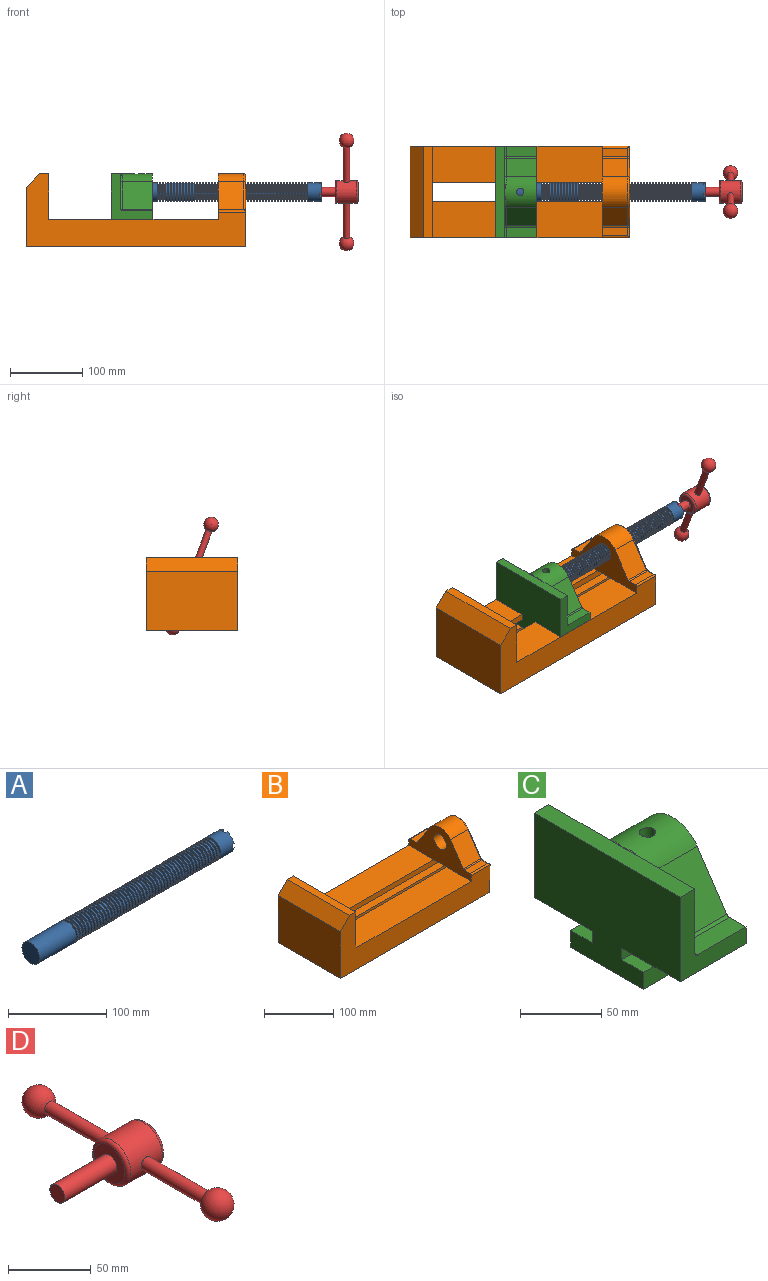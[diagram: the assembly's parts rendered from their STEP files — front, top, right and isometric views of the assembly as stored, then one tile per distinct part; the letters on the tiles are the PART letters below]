
ASSEMBLY  parts=4 mates=3
PART A: 220 faces, bbox 279.4x25.4x25.4 mm
  f0: cylinder r=12.7mm len=25.4mm, axis (-1,0,0), area 1468.2mm2, adj f1,f2,f3,f5,f7,f208,f209,f210
  f1: plane 9.9x9.9mm, normal (1,0,0), area 62.3mm2, adj f0,f4,f213,f216
  f2: plane 9.9x9.9mm, normal (1,0,0), area 62.3mm2, adj f0,f4,f210,f218
  f3: plane 9.9x9.9mm, normal (1,0,0), area 62.3mm2, adj f0,f4,f209,f212
  f4: cylinder r=6.35mm len=25.4mm, axis (1,0,0), area 960.3mm2, adj f1,f2,f3,f5,f6,f208,f209,f210
  f5: plane 9.9x9.9mm, normal (1,0,0), area 62.3mm2, adj f0,f4,f215,f217
  f6: plane 12.7x12.7mm, normal (1,0,0), area 126.7mm2, adj f4
  f7: cone r=12.7mm half-angle=76deg, axis (1,0,0), area 188mm2, adj f0,f9
  f8: cone r=10.16mm half-angle=76deg, axis (-1,0,0), area 188mm2, adj f9,f10
  f9: cylinder r=10.16mm len=20.32mm, axis (1,0,0), area 81.1mm2, adj f7,f8
  f10: cylinder r=12.7mm len=25.4mm, axis (-1,0,0), area 131.7mm2, adj f8,f11
  f11: cone r=12.7mm half-angle=76deg, axis (1,0,0), area 188mm2, adj f10,f13
  f12: cone r=10.16mm half-angle=76deg, axis (-1,0,0), area 188mm2, adj f13,f14
  f13: cylinder r=10.16mm len=20.32mm, axis (1,0,0), area 81.1mm2, adj f11,f12
  f14: cylinder r=12.7mm len=25.4mm, axis (-1,0,0), area 131.7mm2, adj f12,f15
  f15: cone r=12.7mm half-angle=76deg, axis (1,0,0), area 188mm2, adj f14,f17
  f16: cone r=10.16mm half-angle=76deg, axis (-1,0,0), area 188mm2, adj f17,f18
  f17: cylinder r=10.16mm len=20.32mm, axis (1,0,0), area 81.1mm2, adj f15,f16
  f18: cylinder r=12.7mm len=25.4mm, axis (-1,0,0), area 131.7mm2, adj f16,f19
  f19: cone r=12.7mm half-angle=76deg, axis (1,0,0), area 188mm2, adj f18,f21
  f20: cone r=10.16mm half-angle=76deg, axis (-1,0,0), area 188mm2, adj f21,f22
  f21: cylinder r=10.16mm len=20.32mm, axis (1,0,0), area 81.1mm2, adj f19,f20
  f22: cylinder r=12.7mm len=25.4mm, axis (-1,0,0), area 131.7mm2, adj f20,f23
  f23: cone r=12.7mm half-angle=76deg, axis (1,0,0), area 188mm2, adj f22,f25
  f24: cone r=10.16mm half-angle=76deg, axis (-1,0,0), area 188mm2, adj f25,f26
  f25: cylinder r=10.16mm len=20.32mm, axis (1,0,0), area 81.1mm2, adj f23,f24
  f26: cylinder r=12.7mm len=25.4mm, axis (-1,0,0), area 131.7mm2, adj f24,f27
  f27: cone r=12.7mm half-angle=76deg, axis (1,0,0), area 188mm2, adj f26,f29
  f28: cone r=10.16mm half-angle=76deg, axis (-1,0,0), area 188mm2, adj f29,f30
  f29: cylinder r=10.16mm len=20.32mm, axis (1,0,0), area 81.1mm2, adj f27,f28
  f30: cylinder r=12.7mm len=25.4mm, axis (-1,0,0), area 131.7mm2, adj f28,f31
  f31: cone r=12.7mm half-angle=76deg, axis (1,0,0), area 188mm2, adj f30,f33
  f32: cone r=10.16mm half-angle=76deg, axis (-1,0,0), area 188mm2, adj f33,f34
  f33: cylinder r=10.16mm len=20.32mm, axis (1,0,0), area 81.1mm2, adj f31,f32
  f34: cylinder r=12.7mm len=25.4mm, axis (-1,0,0), area 131.7mm2, adj f32,f35
  f35: cone r=12.7mm half-angle=76deg, axis (1,0,0), area 188mm2, adj f34,f37
  f36: cone r=10.16mm half-angle=76deg, axis (-1,0,0), area 188mm2, adj f37,f38
  f37: cylinder r=10.16mm len=20.32mm, axis (1,0,0), area 81.1mm2, adj f35,f36
  f38: cylinder r=12.7mm len=25.4mm, axis (-1,0,0), area 131.7mm2, adj f36,f39
  f39: cone r=12.7mm half-angle=76deg, axis (1,0,0), area 188mm2, adj f38,f41
  f40: cone r=10.16mm half-angle=76deg, axis (-1,0,0), area 188mm2, adj f41,f42
  f41: cylinder r=10.16mm len=20.32mm, axis (1,0,0), area 81.1mm2, adj f39,f40
  f42: cylinder r=12.7mm len=25.4mm, axis (-1,0,0), area 131.7mm2, adj f40,f43
  f43: cone r=12.7mm half-angle=76deg, axis (1,0,0), area 188mm2, adj f42,f45
  f44: cone r=10.16mm half-angle=76deg, axis (-1,0,0), area 188mm2, adj f45,f46
  f45: cylinder r=10.16mm len=20.32mm, axis (1,0,0), area 81.1mm2, adj f43,f44
  f46: cylinder r=12.7mm len=25.4mm, axis (-1,0,0), area 131.7mm2, adj f44,f47
  f47: cone r=12.7mm half-angle=76deg, axis (1,0,0), area 188mm2, adj f46,f49
  f48: cone r=10.16mm half-angle=76deg, axis (-1,0,0), area 188mm2, adj f49,f50
  f49: cylinder r=10.16mm len=20.32mm, axis (1,0,0), area 81.1mm2, adj f47,f48
  f50: cylinder r=12.7mm len=25.4mm, axis (-1,0,0), area 131.7mm2, adj f48,f51
  f51: cone r=12.7mm half-angle=76deg, axis (1,0,0), area 188mm2, adj f50,f53
  f52: cone r=10.16mm half-angle=76deg, axis (-1,0,0), area 188mm2, adj f53,f54
  f53: cylinder r=10.16mm len=20.32mm, axis (1,0,0), area 81.1mm2, adj f51,f52
  f54: cylinder r=12.7mm len=25.4mm, axis (-1,0,0), area 131.7mm2, adj f52,f55
  f55: cone r=12.7mm half-angle=76deg, axis (1,0,0), area 188mm2, adj f54,f57
  f56: cone r=10.16mm half-angle=76deg, axis (-1,0,0), area 188mm2, adj f57,f58
  f57: cylinder r=10.16mm len=20.32mm, axis (1,0,0), area 81.1mm2, adj f55,f56
  f58: cylinder r=12.7mm len=25.4mm, axis (-1,0,0), area 131.7mm2, adj f56,f59
  f59: cone r=12.7mm half-angle=76deg, axis (1,0,0), area 188mm2, adj f58,f61
  f60: cone r=10.16mm half-angle=76deg, axis (-1,0,0), area 188mm2, adj f61,f62
  f61: cylinder r=10.16mm len=20.32mm, axis (1,0,0), area 81.1mm2, adj f59,f60
  f62: cylinder r=12.7mm len=25.4mm, axis (-1,0,0), area 131.7mm2, adj f60,f63
  f63: cone r=12.7mm half-angle=76deg, axis (1,0,0), area 188mm2, adj f62,f65
  f64: cone r=10.16mm half-angle=76deg, axis (-1,0,0), area 188mm2, adj f65,f66
  f65: cylinder r=10.16mm len=20.32mm, axis (1,0,0), area 81.1mm2, adj f63,f64
  f66: cylinder r=12.7mm len=25.4mm, axis (-1,0,0), area 131.7mm2, adj f64,f67
  f67: cone r=12.7mm half-angle=76deg, axis (1,0,0), area 188mm2, adj f66,f69
  f68: cone r=10.16mm half-angle=76deg, axis (-1,0,0), area 188mm2, adj f69,f70
  f69: cylinder r=10.16mm len=20.32mm, axis (1,0,0), area 81.1mm2, adj f67,f68
  f70: cylinder r=12.7mm len=25.4mm, axis (-1,0,0), area 131.7mm2, adj f68,f71
  f71: cone r=12.7mm half-angle=76deg, axis (1,0,0), area 188mm2, adj f70,f73
  f72: cone r=10.16mm half-angle=76deg, axis (-1,0,0), area 188mm2, adj f73,f74
  f73: cylinder r=10.16mm len=20.32mm, axis (1,0,0), area 81.1mm2, adj f71,f72
  f74: cylinder r=12.7mm len=25.4mm, axis (-1,0,0), area 131.7mm2, adj f72,f75
  f75: cone r=12.7mm half-angle=76deg, axis (1,0,0), area 188mm2, adj f74,f77
  f76: cone r=10.16mm half-angle=76deg, axis (-1,0,0), area 188mm2, adj f77,f78
  f77: cylinder r=10.16mm len=20.32mm, axis (1,0,0), area 81.1mm2, adj f75,f76
  f78: cylinder r=12.7mm len=25.4mm, axis (-1,0,0), area 131.7mm2, adj f76,f79
  f79: cone r=12.7mm half-angle=76deg, axis (1,0,0), area 188mm2, adj f78,f81
  f80: cone r=10.16mm half-angle=76deg, axis (-1,0,0), area 188mm2, adj f81,f82
  f81: cylinder r=10.16mm len=20.32mm, axis (1,0,0), area 81.1mm2, adj f79,f80
  f82: cylinder r=12.7mm len=25.4mm, axis (-1,0,0), area 131.7mm2, adj f80,f83
  f83: cone r=12.7mm half-angle=76deg, axis (1,0,0), area 188mm2, adj f82,f85
  f84: cone r=10.16mm half-angle=76deg, axis (-1,0,0), area 188mm2, adj f85,f86
  f85: cylinder r=10.16mm len=20.32mm, axis (1,0,0), area 81.1mm2, adj f83,f84
  f86: cylinder r=12.7mm len=25.4mm, axis (-1,0,0), area 131.7mm2, adj f84,f87
  f87: cone r=12.7mm half-angle=76deg, axis (1,0,0), area 188mm2, adj f86,f89
  f88: cone r=10.16mm half-angle=76deg, axis (-1,0,0), area 188mm2, adj f89,f90
  f89: cylinder r=10.16mm len=20.32mm, axis (1,0,0), area 81.1mm2, adj f87,f88
  f90: cylinder r=12.7mm len=25.4mm, axis (-1,0,0), area 131.7mm2, adj f88,f91
  f91: cone r=12.7mm half-angle=76deg, axis (1,0,0), area 188mm2, adj f90,f93
  f92: cone r=10.16mm half-angle=76deg, axis (-1,0,0), area 188mm2, adj f93,f94
  f93: cylinder r=10.16mm len=20.32mm, axis (1,0,0), area 81.1mm2, adj f91,f92
  f94: cylinder r=12.7mm len=25.4mm, axis (-1,0,0), area 131.7mm2, adj f92,f95
  f95: cone r=12.7mm half-angle=76deg, axis (1,0,0), area 188mm2, adj f94,f97
  f96: cone r=10.16mm half-angle=76deg, axis (-1,0,0), area 188mm2, adj f97,f98
  f97: cylinder r=10.16mm len=20.32mm, axis (1,0,0), area 81.1mm2, adj f95,f96
  f98: cylinder r=12.7mm len=25.4mm, axis (-1,0,0), area 131.7mm2, adj f96,f99
  f99: cone r=12.7mm half-angle=76deg, axis (1,0,0), area 188mm2, adj f98,f101
  f100: cone r=10.16mm half-angle=76deg, axis (-1,0,0), area 188mm2, adj f101,f102
  f101: cylinder r=10.16mm len=20.32mm, axis (1,0,0), area 81.1mm2, adj f99,f100
  f102: cylinder r=12.7mm len=25.4mm, axis (-1,0,0), area 131.7mm2, adj f100,f103
  f103: cone r=12.7mm half-angle=76deg, axis (1,0,0), area 188mm2, adj f102,f105
  f104: cone r=10.16mm half-angle=76deg, axis (-1,0,0), area 188mm2, adj f105,f106
  f105: cylinder r=10.16mm len=20.32mm, axis (1,0,0), area 81.1mm2, adj f103,f104
  f106: cylinder r=12.7mm len=25.4mm, axis (-1,0,0), area 131.7mm2, adj f104,f107
  f107: cone r=12.7mm half-angle=76deg, axis (1,0,0), area 188mm2, adj f106,f109
  f108: cone r=10.16mm half-angle=76deg, axis (-1,0,0), area 188mm2, adj f109,f110
  f109: cylinder r=10.16mm len=20.32mm, axis (1,0,0), area 81.1mm2, adj f107,f108
  f110: cylinder r=12.7mm len=25.4mm, axis (-1,0,0), area 131.7mm2, adj f108,f111
  f111: cone r=12.7mm half-angle=76deg, axis (1,0,0), area 188mm2, adj f110,f113
  f112: cone r=10.16mm half-angle=76deg, axis (-1,0,0), area 188mm2, adj f113,f114
  f113: cylinder r=10.16mm len=20.32mm, axis (1,0,0), area 81.1mm2, adj f111,f112
  f114: cylinder r=12.7mm len=25.4mm, axis (-1,0,0), area 131.7mm2, adj f112,f115
  f115: cone r=12.7mm half-angle=76deg, axis (1,0,0), area 188mm2, adj f114,f117
  f116: cone r=10.16mm half-angle=76deg, axis (-1,0,0), area 188mm2, adj f117,f118
  f117: cylinder r=10.16mm len=20.32mm, axis (1,0,0), area 81.1mm2, adj f115,f116
  f118: cylinder r=12.7mm len=25.4mm, axis (-1,0,0), area 131.7mm2, adj f116,f119
  f119: cone r=12.7mm half-angle=76deg, axis (1,0,0), area 188mm2, adj f118,f121
  f120: cone r=10.16mm half-angle=76deg, axis (-1,0,0), area 188mm2, adj f121,f122
  f121: cylinder r=10.16mm len=20.32mm, axis (1,0,0), area 81.1mm2, adj f119,f120
  f122: cylinder r=12.7mm len=25.4mm, axis (-1,0,0), area 131.7mm2, adj f120,f123
  f123: cone r=12.7mm half-angle=76deg, axis (1,0,0), area 188mm2, adj f122,f125
  f124: cone r=10.16mm half-angle=76deg, axis (-1,0,0), area 188mm2, adj f125,f126
  f125: cylinder r=10.16mm len=20.32mm, axis (1,0,0), area 81.1mm2, adj f123,f124
  f126: cylinder r=12.7mm len=25.4mm, axis (-1,0,0), area 131.7mm2, adj f124,f127
  f127: cone r=12.7mm half-angle=76deg, axis (1,0,0), area 188mm2, adj f126,f129
  f128: cone r=10.16mm half-angle=76deg, axis (-1,0,0), area 188mm2, adj f129,f130
  f129: cylinder r=10.16mm len=20.32mm, axis (1,0,0), area 81.1mm2, adj f127,f128
  f130: cylinder r=12.7mm len=25.4mm, axis (-1,0,0), area 131.7mm2, adj f128,f131
  f131: cone r=12.7mm half-angle=76deg, axis (1,0,0), area 188mm2, adj f130,f133
  f132: cone r=10.16mm half-angle=76deg, axis (-1,0,0), area 188mm2, adj f133,f134
  f133: cylinder r=10.16mm len=20.32mm, axis (1,0,0), area 81.1mm2, adj f131,f132
  f134: cylinder r=12.7mm len=25.4mm, axis (-1,0,0), area 131.7mm2, adj f132,f135
  f135: cone r=12.7mm half-angle=76deg, axis (1,0,0), area 188mm2, adj f134,f137
  f136: cone r=10.16mm half-angle=76deg, axis (-1,0,0), area 188mm2, adj f137,f138
  f137: cylinder r=10.16mm len=20.32mm, axis (1,0,0), area 81.1mm2, adj f135,f136
  f138: cylinder r=12.7mm len=25.4mm, axis (-1,0,0), area 131.7mm2, adj f136,f139
  f139: cone r=12.7mm half-angle=76deg, axis (1,0,0), area 188mm2, adj f138,f141
  f140: cone r=10.16mm half-angle=76deg, axis (-1,0,0), area 188mm2, adj f141,f142
  f141: cylinder r=10.16mm len=20.32mm, axis (1,0,0), area 81.1mm2, adj f139,f140
  f142: cylinder r=12.7mm len=25.4mm, axis (-1,0,0), area 131.7mm2, adj f140,f143
  f143: cone r=12.7mm half-angle=76deg, axis (1,0,0), area 188mm2, adj f142,f145
  f144: cone r=10.16mm half-angle=76deg, axis (-1,0,0), area 188mm2, adj f145,f146
  f145: cylinder r=10.16mm len=20.32mm, axis (1,0,0), area 81.1mm2, adj f143,f144
  f146: cylinder r=12.7mm len=25.4mm, axis (-1,0,0), area 131.7mm2, adj f144,f147
  f147: cone r=12.7mm half-angle=76deg, axis (1,0,0), area 188mm2, adj f146,f149
  f148: cone r=10.16mm half-angle=76deg, axis (-1,0,0), area 188mm2, adj f149,f150
  f149: cylinder r=10.16mm len=20.32mm, axis (1,0,0), area 81.1mm2, adj f147,f148
  f150: cylinder r=12.7mm len=25.4mm, axis (-1,0,0), area 131.7mm2, adj f148,f151
  f151: cone r=12.7mm half-angle=76deg, axis (1,0,0), area 188mm2, adj f150,f153
  f152: cone r=10.16mm half-angle=76deg, axis (-1,0,0), area 188mm2, adj f153,f154
  f153: cylinder r=10.16mm len=20.32mm, axis (1,0,0), area 81.1mm2, adj f151,f152
  f154: cylinder r=12.7mm len=25.4mm, axis (-1,0,0), area 131.7mm2, adj f152,f155
  f155: cone r=12.7mm half-angle=76deg, axis (1,0,0), area 188mm2, adj f154,f157
  f156: cone r=10.16mm half-angle=76deg, axis (-1,0,0), area 188mm2, adj f157,f158
  f157: cylinder r=10.16mm len=20.32mm, axis (1,0,0), area 81.1mm2, adj f155,f156
  f158: cylinder r=12.7mm len=25.4mm, axis (-1,0,0), area 131.7mm2, adj f156,f159
  f159: cone r=12.7mm half-angle=76deg, axis (1,0,0), area 188mm2, adj f158,f161
  f160: cone r=10.16mm half-angle=76deg, axis (-1,0,0), area 188mm2, adj f161,f162
  f161: cylinder r=10.16mm len=20.32mm, axis (1,0,0), area 81.1mm2, adj f159,f160
  f162: cylinder r=12.7mm len=25.4mm, axis (-1,0,0), area 131.7mm2, adj f160,f163
  f163: cone r=12.7mm half-angle=76deg, axis (1,0,0), area 188mm2, adj f162,f165
  f164: cone r=10.16mm half-angle=76deg, axis (-1,0,0), area 188mm2, adj f165,f166
  f165: cylinder r=10.16mm len=20.32mm, axis (1,0,0), area 81.1mm2, adj f163,f164
  f166: cylinder r=12.7mm len=25.4mm, axis (-1,0,0), area 131.7mm2, adj f164,f167
  f167: cone r=12.7mm half-angle=76deg, axis (1,0,0), area 188mm2, adj f166,f169
  f168: cone r=10.16mm half-angle=76deg, axis (-1,0,0), area 188mm2, adj f169,f170
  f169: cylinder r=10.16mm len=20.32mm, axis (1,0,0), area 81.1mm2, adj f167,f168
  f170: cylinder r=12.7mm len=25.4mm, axis (-1,0,0), area 131.7mm2, adj f168,f171
  f171: cone r=12.7mm half-angle=76deg, axis (1,0,0), area 188mm2, adj f170,f173
  f172: cone r=10.16mm half-angle=76deg, axis (-1,0,0), area 188mm2, adj f173,f174
  f173: cylinder r=10.16mm len=20.32mm, axis (1,0,0), area 81.1mm2, adj f171,f172
  f174: cylinder r=12.7mm len=25.4mm, axis (-1,0,0), area 131.7mm2, adj f172,f175
  f175: cone r=12.7mm half-angle=76deg, axis (1,0,0), area 188mm2, adj f174,f177
  f176: cone r=10.16mm half-angle=76deg, axis (-1,0,0), area 188mm2, adj f177,f178
  f177: cylinder r=10.16mm len=20.32mm, axis (1,0,0), area 81.1mm2, adj f175,f176
  f178: cylinder r=12.7mm len=25.4mm, axis (-1,0,0), area 131.7mm2, adj f176,f179
  f179: cone r=12.7mm half-angle=76deg, axis (1,0,0), area 188mm2, adj f178,f181
  f180: cone r=10.16mm half-angle=76deg, axis (-1,0,0), area 188mm2, adj f181,f182
  f181: cylinder r=10.16mm len=20.32mm, axis (1,0,0), area 81.1mm2, adj f179,f180
  f182: cylinder r=12.7mm len=25.4mm, axis (-1,0,0), area 131.7mm2, adj f180,f183
  f183: cone r=12.7mm half-angle=76deg, axis (1,0,0), area 188mm2, adj f182,f185
  f184: cone r=10.16mm half-angle=76deg, axis (-1,0,0), area 188mm2, adj f185,f186
  f185: cylinder r=10.16mm len=20.32mm, axis (1,0,0), area 81.1mm2, adj f183,f184
  f186: cylinder r=12.7mm len=25.4mm, axis (-1,0,0), area 131.7mm2, adj f184,f187
  f187: cone r=12.7mm half-angle=76deg, axis (1,0,0), area 188mm2, adj f186,f189
  f188: cone r=10.16mm half-angle=76deg, axis (-1,0,0), area 188mm2, adj f189,f190
  f189: cylinder r=10.16mm len=20.32mm, axis (1,0,0), area 81.1mm2, adj f187,f188
  f190: cylinder r=12.7mm len=25.4mm, axis (-1,0,0), area 131.7mm2, adj f188,f191
  f191: cone r=12.7mm half-angle=76deg, axis (1,0,0), area 188mm2, adj f190,f193
  f192: cone r=10.16mm half-angle=76deg, axis (-1,0,0), area 188mm2, adj f193,f194
  f193: cylinder r=10.16mm len=20.32mm, axis (1,0,0), area 81.1mm2, adj f191,f192
  f194: cylinder r=12.7mm len=25.4mm, axis (-1,0,0), area 131.7mm2, adj f192,f195
  f195: cone r=12.7mm half-angle=76deg, axis (1,0,0), area 188mm2, adj f194,f197
  f196: cone r=10.16mm half-angle=76deg, axis (-1,0,0), area 188mm2, adj f197,f198
  f197: cylinder r=10.16mm len=20.32mm, axis (1,0,0), area 81.1mm2, adj f195,f196
  f198: cylinder r=12.7mm len=25.4mm, axis (-1,0,0), area 131.7mm2, adj f196,f199
  f199: cone r=12.7mm half-angle=76deg, axis (1,0,0), area 188mm2, adj f198,f201
  f200: cone r=10.16mm half-angle=76deg, axis (-1,0,0), area 188mm2, adj f201,f202
  f201: cylinder r=10.16mm len=20.32mm, axis (1,0,0), area 81.1mm2, adj f199,f200
  f202: cylinder r=12.7mm len=25.4mm, axis (-1,0,0), area 131.7mm2, adj f200,f203
  f203: cone r=12.7mm half-angle=76deg, axis (1,0,0), area 188mm2, adj f202,f205
  f204: cone r=10.16mm half-angle=76deg, axis (-1,0,0), area 188mm2, adj f205,f207
  f205: cylinder r=10.16mm len=20.32mm, axis (1,0,0), area 81.1mm2, adj f203,f204
  f206: plane 25.4x25.4mm, normal (-1,0,0), area 506.7mm2, adj f207
  f207: cylinder r=12.7mm len=52.45mm, axis (-1,0,0), area 4185.4mm2, adj f204,f206
  f208: plane 6.88x5.08mm, normal (1,0,0), area 32.7mm2, adj f0,f4,f209,f210
  f209: plane 6.62x2.54mm, normal (0,-1,0), area 16.8mm2, adj f0,f3,f4,f208
  f210: plane 6.62x2.54mm, normal (0,1,0), area 16.8mm2, adj f0,f2,f4,f208
  f211: plane 6.88x5.08mm, normal (1,0,0), area 32.7mm2, adj f0,f4,f212,f213
  f212: plane 6.62x2.54mm, normal (0,0,1), area 16.8mm2, adj f0,f3,f4,f211
  f213: plane 6.62x2.54mm, normal (0,0,-1), area 16.8mm2, adj f0,f1,f4,f211
  f214: plane 6.88x5.08mm, normal (1,0,0), area 32.7mm2, adj f0,f4,f215,f216
  f215: plane 6.62x2.54mm, normal (0,1,0), area 16.8mm2, adj f0,f4,f5,f214
  f216: plane 6.62x2.54mm, normal (0,-1,0), area 16.8mm2, adj f0,f1,f4,f214
  f217: plane 6.62x2.54mm, normal (0,0,-1), area 16.8mm2, adj f0,f4,f5,f219
  f218: plane 6.62x2.54mm, normal (0,0,1), area 16.8mm2, adj f0,f2,f4,f219
  f219: plane 6.88x5.08mm, normal (1,0,0), area 32.7mm2, adj f0,f4,f217,f218
PART B: 39 faces, bbox 304.8x127x103.7 mm
  f0: plane 234.95x50.8mm, normal (0,0,1), area 11935.5mm2, adj f3,f8,f16,f26
  f1: plane 127x99.06mm, normal (1,0,0), area 7097.5mm2, adj f7,f8,f9,f14,f17,f18,f19,f20
  f2: plane 234.95x50.8mm, normal (0,0,1), area 11935.5mm2, adj f3,f9,f16,f27
  f3: plane 127x101.6mm, normal (1,0,0), area 9516.1mm2, adj f0,f2,f4,f7,f8,f9,f18,f19
  f4: plane 127x12.7mm, normal (0,0,1), area 1612.9mm2, adj f3,f5,f8,f9
  f5: plane 127x19.05mm, normal (-0.71,0,0.71), area 3421.5mm2, adj f4,f6,f8,f9
  f6: plane 127x82.55mm, normal (-1,0,0), area 10483.8mm2, adj f5,f7,f8,f9
  f7: plane 304.8x127mm, normal (0,0,-1), area 31774.1mm2, adj f1,f3,f6,f8,f9,f21,f22
  f8: plane 304.8x101.6mm, normal (0,-1,0), area 13834.6mm2, adj f0,f1,f3,f4,f5,f6,f7,f16
  f9: plane 304.8x101.6mm, normal (0,1,0), area 13834.6mm2, adj f1,f2,f3,f4,f5,f6,f7,f16
  f10: plane 35.56x11.98mm, normal (0,0,1), area 426mm2, adj f16,f28,f29,f30
  f11: plane 38.43x35.56mm, normal (0,0.83,0.56), area 1645.4mm2, adj f12,f16,f29,f32
  f12: cylinder r=25.4mm len=42.19mm, axis (1,0,0), area 1770.2mm2, adj f11,f13,f16,f33
  f13: plane 38.43x35.56mm, normal (0,-0.83,0.56), area 1645.4mm2, adj f12,f16,f34,f35
  f14: cylinder r=12.7mm len=38.1mm, axis (1,0,0), area 3040.2mm2, adj f1,f16
  f15: plane 35.56x11.98mm, normal (0,0,1), area 426mm2, adj f16,f34,f36,f38
  f16: plane 127x63.5mm, normal (-1,0,0), area 4155.5mm2, adj f0,f2,f8,f9,f10,f11,f12,f13
  f17: plane 38.1x25.4mm, normal (0,0,-1), area 967.7mm2, adj f1,f16,f26,f27
  f18: plane 273.05x19.05mm, normal (0,0,-1), area 5201.6mm2, adj f1,f3,f19,f26
  f19: plane 273.05x12.7mm, normal (0,1,0), area 3467.7mm2, adj f1,f3,f18,f20
  f20: plane 273.05x19.05mm, normal (0,0,1), area 5201.6mm2, adj f1,f3,f19,f21
  f21: plane 273.05x16.51mm, normal (0,1,0), area 4508.1mm2, adj f1,f3,f7,f20
  f22: plane 273.05x16.51mm, normal (0,-1,0), area 4508.1mm2, adj f1,f3,f7,f23
  f23: plane 273.05x19.05mm, normal (0,0,1), area 5201.6mm2, adj f1,f3,f22,f24
  f24: plane 273.05x12.7mm, normal (0,-1,0), area 3467.7mm2, adj f1,f3,f23,f25
  f25: plane 273.05x19.05mm, normal (0,0,-1), area 5201.6mm2, adj f1,f3,f24,f27
  f26: plane 273.05x8.89mm, normal (0,1,0), area 2427.4mm2, adj f0,f1,f3,f17,f18
  f27: plane 273.05x8.89mm, normal (0,-1,0), area 2427.4mm2, adj f1,f2,f3,f17,f25
  f28: cylinder r=2.54mm len=38.1mm, axis (1,0,0), area 148.3mm2, adj f9,f10,f16,f30
  f29: cylinder r=2.54mm len=35.56mm, axis (-1,0,0), area 88.5mm2, adj f10,f11,f16,f31
  f30: cylinder r=2.54mm len=14.52mm, axis (0,1,0), area 54.3mm2, adj f1,f10,f28,f31
  f31: torus R=5.08mm, axis (-1,0,0), area 13.5mm2, adj f1,f29,f30,f32
  f32: cylinder r=2.54mm len=39.84mm, axis (0,0.56,-0.83), area 184.6mm2, adj f1,f11,f31,f33
  f33: torus R=22.86mm, axis (-1,0,0), area 191.4mm2, adj f1,f12,f32,f35
  f34: cylinder r=2.54mm len=35.56mm, axis (-1,0,0), area 88.5mm2, adj f13,f15,f16,f37
  f35: cylinder r=2.54mm len=39.84mm, axis (0,0.56,0.83), area 184.6mm2, adj f1,f13,f33,f37
  f36: cylinder r=2.54mm len=38.1mm, axis (-1,0,0), area 148.3mm2, adj f8,f15,f16,f38
  f37: torus R=5.08mm, axis (-1,0,0), area 13.5mm2, adj f1,f34,f35,f38
  f38: cylinder r=2.54mm len=14.52mm, axis (0,1,0), area 54.3mm2, adj f1,f15,f36,f37
PART C: 36 faces, bbox 57.2x127x89 mm
  f0: plane 57.15x50.8mm, normal (0,0,-1), area 2903.2mm2, adj f6,f9,f10,f23
  f1: cylinder r=12.7mm len=44.45mm, axis (1,0,0), area 3464.3mm2, adj f6,f15,f16
  f2: plane 41.91x14.52mm, normal (0,0,1), area 608.5mm2, adj f6,f11,f24,f25
  f3: plane 51.86x48.26mm, normal (1,0,0), area 1495.7mm2, adj f8,f10,f31,f33,f35
  f4: plane 51.86x48.26mm, normal (1,0,0), area 1495.7mm2, adj f8,f11,f24,f28,f29
  f5: plane 57.15x50.8mm, normal (0,0,-1), area 2903.2mm2, adj f6,f9,f11,f22
  f6: plane 127x85.09mm, normal (1,0,0), area 5190.6mm2, adj f0,f1,f2,f5,f7,f10,f11,f12
  f7: plane 41.91x14.52mm, normal (0,0,1), area 608.5mm2, adj f6,f10,f30,f31
  f8: plane 127x12.7mm, normal (0,0,1), area 1612.9mm2, adj f3,f4,f9,f10,f11,f26,f34
  f9: plane 127x85.09mm, normal (-1,0,0), area 9096.8mm2, adj f0,f5,f8,f10,f11,f17,f18,f19
  f10: plane 63.5x57.15mm, normal (0,-1,0), area 1372.3mm2, adj f0,f3,f6,f7,f8,f9,f31
  f11: plane 63.5x57.15mm, normal (0,1,0), area 1372.3mm2, adj f2,f4,f5,f6,f8,f9,f24
  f12: plane 41.91x38.43mm, normal (0,-0.83,0.56), area 1939.2mm2, adj f6,f13,f30,f33
  f13: cylinder r=25.4mm len=44.45mm, axis (1,0,0), area 2026.5mm2, adj f6,f12,f14,f16,f26,f28,f34,f35
  f14: plane 41.91x38.43mm, normal (0,0.83,0.56), area 1939.2mm2, adj f6,f13,f25,f29
  f15: plane 25.4x25.4mm, normal (1,0,0), area 506.7mm2, adj f1
  f16: cylinder r=5.08mm len=13.76mm, axis (0,0,1), area 414mm2, adj f1,f13
  f17: plane 57.15x19.05mm, normal (0,0,1), area 1088.7mm2, adj f6,f9,f18,f23
  f18: plane 57.15x12.7mm, normal (0,-1,0), area 725.8mm2, adj f6,f9,f17,f19
  f19: plane 63.5x57.15mm, normal (0,0,-1), area 3629mm2, adj f6,f9,f18,f20
  f20: plane 57.15x12.7mm, normal (0,1,0), area 725.8mm2, adj f6,f9,f19,f21
  f21: plane 57.15x19.05mm, normal (0,0,1), area 1088.7mm2, adj f6,f9,f20,f22
  f22: plane 57.15x8.89mm, normal (0,1,0), area 508.1mm2, adj f5,f6,f9,f21
  f23: plane 57.15x8.89mm, normal (0,-1,0), area 508.1mm2, adj f0,f6,f9,f17
  f24: cylinder r=2.54mm len=14.52mm, axis (0,-1,0), area 57.9mm2, adj f2,f4,f11,f27
  f25: cylinder r=2.54mm len=41.91mm, axis (1,0,0), area 104.3mm2, adj f2,f6,f14,f27
  f26: bspline ~12.24x2.8mm, area 20.9mm2, adj f8,f13,f28
  f27: sphere r=2.54mm, area 6.3mm2, adj f24,f25,f29
  f28: torus R=27.94mm, axis (1,0,0), area 57.8mm2, adj f4,f13,f26,f29
  f29: cylinder r=2.54mm len=39.84mm, axis (0,-0.56,0.83), area 184.6mm2, adj f4,f14,f27,f28
  f30: cylinder r=2.54mm len=41.91mm, axis (1,0,0), area 104.3mm2, adj f6,f7,f12,f32
  f31: cylinder r=2.54mm len=14.52mm, axis (0,-1,0), area 57.9mm2, adj f3,f7,f10,f32
  f32: sphere r=2.54mm, area 6.3mm2, adj f30,f31,f33
  f33: cylinder r=2.54mm len=39.84mm, axis (0,-0.56,-0.83), area 184.6mm2, adj f3,f12,f32,f35
  f34: bspline ~12.24x2.8mm, area 20.9mm2, adj f8,f13,f35
  f35: torus R=27.94mm, axis (1,0,0), area 57.8mm2, adj f3,f13,f33,f34
PART D: 11 faces, bbox 76.2x172.7x34.4 mm
  f0: sphere r=10.16mm, area 1231.8mm2, adj f1
  f1: cylinder r=4.45mm len=51.82mm, axis (0,1,0), area 1438.5mm2, adj f0,f4
  f2: sphere r=10.16mm, area 1231.8mm2, adj f3
  f3: cylinder r=4.45mm len=51.82mm, axis (0,1,0), area 1438.5mm2, adj f2,f4
  f4: cylinder r=15.88mm len=31.75mm, axis (-1,0,0), area 2534.7mm2, adj f1,f3,f9,f10
  f5: cylinder r=6.35mm len=44.45mm, axis (-1,0,0), area 1773.5mm2, adj f6,f8
  f6: plane 12.7x12.7mm, normal (-1,0,0), area 126.7mm2, adj f5
  f7: plane 26.67x26.67mm, normal (1,0,0), area 558.6mm2, adj f10
  f8: plane 26.67x26.67mm, normal (-1,0,0), area 432mm2, adj f5,f9
  f9: torus R=13.33mm, axis (1,0,0), area 374.8mm2, adj f4,f8
  f10: torus R=13.33mm, axis (1,0,0), area 374.8mm2, adj f4,f7
PLACE A rot(axis=(-1,0,0),69.6deg) t=(86.32,-71.42,49.65)mm
PLACE B at identity fixed
PLACE C t=(86.32,0,0)mm
PLACE D rot(axis=(-1,0,0),69.6deg) t=(86.32,-71.42,49.65)mm
MATE revolute C.f28 <-> A.f7  axis (1,0,0) through (-174.03,0,76.2)mm
MATE fastened D.f5 <-> A.f7  axis (-1,0,0) through (79.97,0,76.2)mm
MATE slider B.f3 <-> C.f9  axis (-1,0,0) through (-273.05,-63.5,38.1)mm
